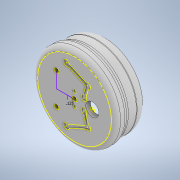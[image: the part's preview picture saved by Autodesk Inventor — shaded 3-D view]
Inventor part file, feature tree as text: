
AUTODESK INVENTOR PART (.ipt)
format: ipt  version: 2022 (Build 260153000, 153)  size: 311,808 bytes
history: native  units: in
note: dims shown in document units (in); Inventor stores cm internally (conversion verified against a paired STEP export)
features: sketch x7, extrude x6, fillet x4, revolve x1, projected_geometry x1
ambient origin geometry x8: Origin, YZ Plane, XZ Plane, XY Plane, X Axis, Y Axis, Z Axis, Center Point
bodies: Solid1 (feature_tree)
feature tree (19):
  sketch  "Sketch1"  dims[d0=1.9685in d1=0.3543in]
  extrude  "Extrusion1"  Depth=0.3543in
  extrude  "Extrusion2"  Depth=0.0787in
  extrude  "Extrusion4"  Depth=0.125in
  fillet  "Fillet2"  Radius=0.7087in
  sketch  "Sketch5"  dims[d4=0.125in d5=0.0in d6=0.125in d7=0.7087in d8=0.0in]
  extrude  "Extrusion5"  Depth=0.7087in TaperAngle=0.0deg
  extrude  "Extrusion6"  Depth=0.12in
  sketch  "Sketch6"  dims[d16=0.12in d17=0.7087in d18=0.0in]
  revolve  "Revolution1"  [1 undecoded]
  fillet  "Fillet3"  Radius=0.12in
  sketch  "Sketch8"  dims[d21=0.42in d22=0.48in d23=0.12in]
  extrude  "Extrusion7"  Depth=0.12in
  fillet  "Fillet4"  Radius=0.48in
  fillet  "Fillet5"  Radius=0.42in
  sketch  "Sketch4"  dims[d2=0.0787in d3=0.0787in]
  sketch  "Sketch7"  dims[d19=0.125in d20=0.12in]
  projected_geometry  "Projected Loop3"
  sketch  "Sketch9"  dims[d24=0.48in d25=0.12in d26=0.48in d27=0.42in d28=0.1575in d29=0.1575in d30=0.1575in d31=0.215in d32=0.73in d33=0.35in d34=0.48in d35=0.33in d36=0.1in d37=0.0394in d38=0.0394in d39=0.0in d40=0.0in d41=0.0394in d42=0.0in d44=0.15in d45=0.3in d46=0.0394in d47=90.0deg d48=0.125in d49=0.125in d50=0.35in d51=1.0in d52=0.0in d53=0.25in d54=0.25in]
note: 1 required parameter value undecoded (feature->parameter linkage not recoverable at this tier; creation-order binding heuristic only, values carry confidence <= 0.55)
